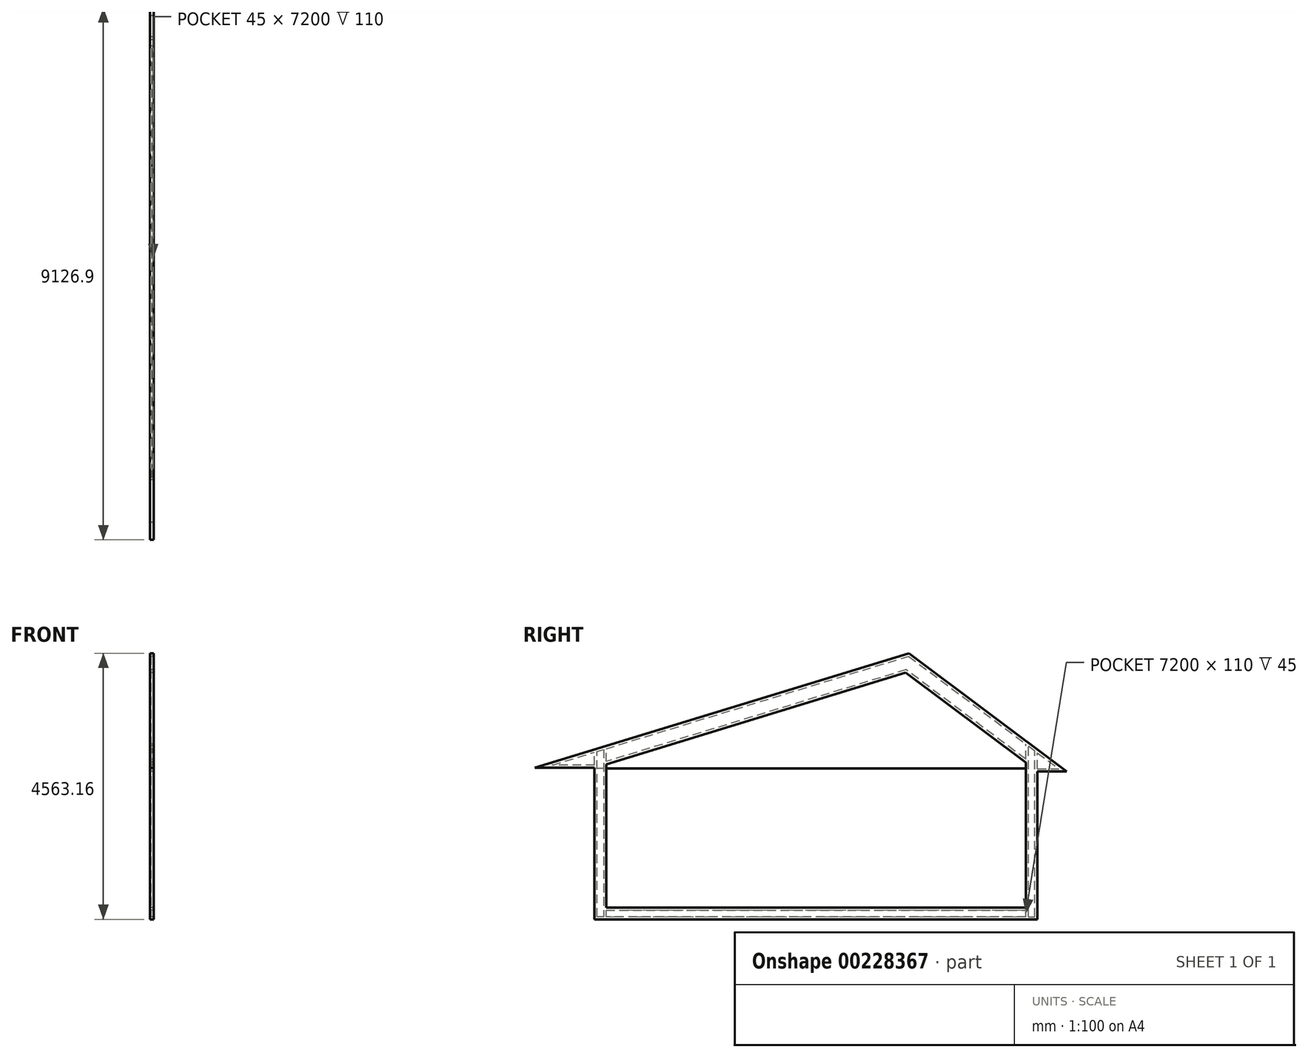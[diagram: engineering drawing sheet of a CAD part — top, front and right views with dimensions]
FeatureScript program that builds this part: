
annotation { "Feature Type Name" : "Feature", "Feature Type Description" : "" }
export const myFeature = defineFeature(function(context is Context, id is Id, definition is map)
    precondition{}
    {
        {
            var Q0;
            Q0=qCreatedBy(makeId("Right.planeOp"),FACE);
            var sketch = newSketch(context, id + "F0", { "sketchPlane" : qUnion([Q0])});
            skLineSegment(sketch, "E0", {"start": v(0, 0) * mm, "end": v(0, 2913.7) * mm});
            skLineSegment(sketch, "E1", {"start": v(0, 2913.7) * mm, "end": v(5395.13, 4563.16) * mm});
            skLineSegment(sketch, "E2", {"start": v(5395.13, 4563.16) * mm, "end": v(7600, 2913.7) * mm});
            skLineSegment(sketch, "E3", {"start": v(7600, 2913.7) * mm, "end": v(7600, 0) * mm});
            skLineSegment(sketch, "E4", {"start": v(7600, 0) * mm, "end": v(0, 0) * mm});
            skLineSegment(sketch, "E5", {"start": v(200, 200) * mm, "end": v(200, 2661.15) * mm});
            skLineSegment(sketch, "E6", {"start": v(200, 2661.15) * mm, "end": v(5337.3, 4231.77) * mm});
            skLineSegment(sketch, "E7", {"start": v(5337.3, 4231.77) * mm, "end": v(7400, 2688.67) * mm});
            skLineSegment(sketch, "E8", {"start": v(7400, 2688.67) * mm, "end": v(7400, 200) * mm});
            skLineSegment(sketch, "E9", {"start": v(7400, 200) * mm, "end": v(200, 200) * mm});
            skLineSegment(sketch, "E10", {"start": v(0, 2913.7) * mm, "end": v(-1026.1, 2600) * mm});
            skLineSegment(sketch, "E11", {"start": v(-1026.1, 2600) * mm, "end": v(0, 2600) * mm});
            skLineSegment(sketch, "E12", {"start": v(7600, 2913.7) * mm, "end": v(8100.81, 2539.05) * mm});
            skLineSegment(sketch, "E13", {"start": v(8100.81, 2539.05) * mm, "end": v(7600, 2539.05) * mm});
            skSolve(sketch);
        }
        {
            var Q0;
            Q0 = qSketchRegion(id + "F0", true);
            extrude(context, id + "F1", {"entities" : qUnion([Q0]), "depth" : 10 * mm, "offsetDistance" : 25 * mm});
        }
        {
            var Q0;
            Q0=makeQuery(id+"F1.opExtrude","CAP_FACE",FACE,{"disambiguationData":[OSD([sQuery(id+"F0.wireOp",EDGE,"E0"),sQuery(id+"F0.wireOp",EDGE,"E1"),sQuery(id+"F0.wireOp",EDGE,"E2"),sQuery(id+"F0.wireOp",EDGE,"E3"),sQuery(id+"F0.wireOp",EDGE,"E4"),sQuery(id+"F0.wireOp",EDGE,"E5"),sQuery(id+"F0.wireOp",EDGE,"E6"),sQuery(id+"F0.wireOp",EDGE,"E7"),sQuery(id+"F0.wireOp",EDGE,"E8"),sQuery(id+"F0.wireOp",EDGE,"E9"),sQuery(id+"F0.wireOp",EDGE,"E10"),sQuery(id+"F0.wireOp",EDGE,"E11"),sQuery(id+"F0.wireOp",EDGE,"E12"),sQuery(id+"F0.wireOp",EDGE,"E13")])],"isStart":false});
            var sketch = newSketch(context, id + "F2", { "sketchPlane" : qUnion([Q0])});
            skLineSegment(sketch, "E14", {"start": v(-872.18, 2600) * mm, "end": v(5386.45, 4513.45) * mm});
            skLineSegment(sketch, "E15", {"start": v(5386.45, 4513.45) * mm, "end": v(8025.7, 2539.05) * mm});
            skLineSegment(sketch, "E16", {"start": v(45, 0) * mm, "end": v(45, 2880.4) * mm});
            skLineSegment(sketch, "E17", {"start": v(155, 2914.04) * mm, "end": v(155, 0) * mm});
            skLineSegment(sketch, "E18", {"start": v(7445, 0) * mm, "end": v(7445, 2973.46) * mm});
            skLineSegment(sketch, "E19", {"start": v(200, 0) * mm, "end": v(200, 2927.8) * mm});
            skLineSegment(sketch, "E20", {"start": v(7400, 0) * mm, "end": v(7400, 3007.13) * mm});
            skLineSegment(sketch, "E21", {"start": v(7555, 0) * mm, "end": v(7555, 2891.17) * mm});
            skLineSegment(sketch, "E22", {"start": v(7600, 2539.05) * mm, "end": v(7600, 2857.5) * mm});
            skLineSegment(sketch, "E23", {"start": v(0, 2600) * mm, "end": v(0, 2866.65) * mm});
            skLineSegment(sketch, "E24", {"start": v(0, 2645) * mm, "end": v(-724.99, 2645) * mm});
            skLineSegment(sketch, "E25", {"start": v(7600, 2584.05) * mm, "end": v(7965.54, 2584.05) * mm});
            skLineSegment(sketch, "E26", {"start": v(7400, 2744.87) * mm, "end": v(5345.97, 4281.48) * mm});
            skLineSegment(sketch, "E27", {"start": v(5345.97, 4281.48) * mm, "end": v(200, 2708.2) * mm});
            skLineSegment(sketch, "E28", {"start": v(200, 155) * mm, "end": v(7400, 155) * mm});
            skLineSegment(sketch, "E29", {"start": v(7400, 45) * mm, "end": v(200, 45) * mm});
            skLineSegment(sketch, "E30", {"start": v(5337.3, 4231.77) * mm, "end": v(5345.97, 4281.48) * mm});
            skLineSegment(sketch, "E31", {"start": v(5386.45, 4513.45) * mm, "end": v(5395.13, 4563.16) * mm});
            skLineSegment(sketch, "E32", {"start": v(155, 45) * mm, "end": v(45, 45) * mm});
            skLineSegment(sketch, "E33", {"start": v(7400, 45) * mm, "end": v(7555, 45) * mm});
            skSolve(sketch);
        }
        {
            var Q0;
            {var subQ3=sQuery(id+"F2.wireOp",EDGE,"E24");Q0=makeQuery(id+"F2.imprint","IMPRINT",FACE,{"disambiguationData":[TD([[makeQuery(id+"F2.imprint","IMPRINT",EDGE,{"derivedFrom":subQ3}),1.0]])]});}
            var Q1;
            {var subQ8=sQuery(id+"F2.wireOp",EDGE,"E31");Q1=makeQuery(id+"F2.imprint","IMPRINT",FACE,{"disambiguationData":[TD([[makeQuery(id+"F2.imprint","IMPRINT",EDGE,{"derivedFrom":subQ8}),1.0]])]});}
            var Q2;
            {var subQ5=sQuery(id+"F2.wireOp",EDGE,"E16");Q2=makeQuery(id+"F2.imprint","IMPRINT",FACE,{"disambiguationData":[TD([[makeQuery(id+"F2.imprint","IMPRINT",EDGE,{"derivedFrom":subQ5}),1.0]])]});}
            var Q3;
            {var subQ5=sQuery(id+"F2.wireOp",EDGE,"E17");Q3=makeQuery(id+"F2.imprint","IMPRINT",FACE,{"disambiguationData":[TD([[makeQuery(id+"F2.imprint","IMPRINT",EDGE,{"derivedFrom":subQ5}),1.0]])]});}
            var Q4;
            {var subQ2=sQuery(id+"F2.wireOp",EDGE,"E27");Q4=makeQuery(id+"F2.imprint","IMPRINT",FACE,{"disambiguationData":[TD([[makeQuery(id+"F2.imprint","IMPRINT",EDGE,{"derivedFrom":subQ2}),1.0]])]});}
            var Q5;
            {var subQ2=sQuery(id+"F2.wireOp",EDGE,"E28");Q5=makeQuery(id+"F2.imprint","IMPRINT",FACE,{"disambiguationData":[TD([[makeQuery(id+"F2.imprint","IMPRINT",EDGE,{"derivedFrom":subQ2}),1.0]])]});}
            var Q6;
            {var subQ3=sQuery(id+"F2.wireOp",EDGE,"E29");Q6=makeQuery(id+"F2.imprint","IMPRINT",FACE,{"disambiguationData":[TD([[makeQuery(id+"F2.imprint","IMPRINT",EDGE,{"derivedFrom":subQ3}),1.0]])]});}
            var Q7;
            {var subQ2=sQuery(id+"F2.wireOp",EDGE,"E26");Q7=makeQuery(id+"F2.imprint","IMPRINT",FACE,{"disambiguationData":[TD([[makeQuery(id+"F2.imprint","IMPRINT",EDGE,{"derivedFrom":subQ2}),1.0]])]});}
            var Q8;
            {var subQ6=sQuery(id+"F2.wireOp",EDGE,"E31");Q8=makeQuery(id+"F2.imprint","IMPRINT",FACE,{"disambiguationData":[TD([[makeQuery(id+"F2.imprint","IMPRINT",EDGE,{"derivedFrom":subQ6}),-1.0]])]});}
            var Q9;
            {var subQ4=sQuery(id+"F2.wireOp",EDGE,"E18");Q9=makeQuery(id+"F2.imprint","IMPRINT",FACE,{"disambiguationData":[TD([[makeQuery(id+"F2.imprint","IMPRINT",EDGE,{"derivedFrom":subQ4}),1.0]])]});}
            var Q10;
            {var subQ3=sQuery(id+"F2.wireOp",EDGE,"E21");Q10=makeQuery(id+"F2.imprint","IMPRINT",FACE,{"disambiguationData":[TD([[makeQuery(id+"F2.imprint","IMPRINT",EDGE,{"derivedFrom":subQ3}),-1.0]])]});}
            var Q11;
            {var subQ3=sQuery(id+"F2.wireOp",EDGE,"E25");Q11=makeQuery(id+"F2.imprint","IMPRINT",FACE,{"disambiguationData":[TD([[makeQuery(id+"F2.imprint","IMPRINT",EDGE,{"derivedFrom":subQ3}),-1.0]])]});}
            var Q12;
            {var subQ5=sQuery(id+"F2.wireOp",EDGE,"E18");var subQ6=sQuery(id+"F2.wireOp",EDGE,"E15");var subQ7=makeQuery(id+"F2.imprint","INTERSECT",VERTEX,{"derivedFrom":[subQ6,subQ5]});Q12=makeQuery(id+"F2.imprint","IMPRINT",FACE,{"disambiguationData":[TD([[makeQuery(id+"F2.imprint","IMPRINT",EDGE,{"disambiguationData":[TD([[subQ7,1.0]])],"derivedFrom":subQ6}),-1.0]])]});}
            var Q13;
            {var subQ0=sQuery(id+"F2.wireOp",EDGE,"E18");var subQ1=makeQuery(id+"F1.opExtrude","CAP_EDGE",EDGE,{"disambiguationData":[OSD([sQuery(id+"F0.wireOp",EDGE,"E4")])],"isStart":false});var subQ2=makeQuery(id+"F2.imprint","INTERSECT",VERTEX,{"derivedFrom":[subQ1,subQ0]});Q13=makeQuery(id+"F2.imprint","IMPRINT",FACE,{"disambiguationData":[TD([[makeQuery(id+"F2.imprint","IMPRINT",EDGE,{"disambiguationData":[TD([[subQ2,-1.0]])],"derivedFrom":subQ0}),-1.0]])]});}
            var Q14;
            {var subQ3=sQuery(id+"F2.wireOp",EDGE,"E32");Q14=makeQuery(id+"F2.imprint","IMPRINT",FACE,{"disambiguationData":[TD([[makeQuery(id+"F2.imprint","IMPRINT",EDGE,{"derivedFrom":subQ3}),1.0]])]});}
            extrude(context, id + "F3", {"entities" : qUnion([Q0, Q1, Q2, Q3, Q4, Q5, Q6, Q7, Q8, Q9, Q10, Q11, Q12, Q13, Q14]), "operationType" : NewBodyOperationType.ADD, "depth" : 45 * mm, "offsetDistance" : 25 * mm});
        }
        {
            var Q0;
            Q0=makeQuery(id+"F3.opExtrude","CAP_FACE",FACE,{"disambiguationData":[OSD([sQuery(id+"F0.wireOp",EDGE,"E0"),sQuery(id+"F0.wireOp",EDGE,"E1"),sQuery(id+"F0.wireOp",EDGE,"E2"),sQuery(id+"F0.wireOp",EDGE,"E3"),sQuery(id+"F0.wireOp",EDGE,"E4"),sQuery(id+"F0.wireOp",EDGE,"E6"),sQuery(id+"F0.wireOp",EDGE,"E7"),sQuery(id+"F0.wireOp",EDGE,"E9"),sQuery(id+"F0.wireOp",EDGE,"E10"),sQuery(id+"F0.wireOp",EDGE,"E11"),sQuery(id+"F0.wireOp",EDGE,"E12"),sQuery(id+"F0.wireOp",EDGE,"E13"),sQuery(id+"F2.wireOp",EDGE,"E14"),sQuery(id+"F2.wireOp",EDGE,"E15"),sQuery(id+"F2.wireOp",EDGE,"E16"),sQuery(id+"F2.wireOp",EDGE,"E17"),sQuery(id+"F2.wireOp",EDGE,"E18"),sQuery(id+"F2.wireOp",EDGE,"E19"),sQuery(id+"F2.wireOp",EDGE,"E20"),sQuery(id+"F2.wireOp",EDGE,"E21"),sQuery(id+"F2.wireOp",EDGE,"E22"),sQuery(id+"F2.wireOp",EDGE,"E23"),sQuery(id+"F2.wireOp",EDGE,"E24"),sQuery(id+"F2.wireOp",EDGE,"E25"),sQuery(id+"F2.wireOp",EDGE,"E26"),sQuery(id+"F2.wireOp",EDGE,"E27"),sQuery(id+"F2.wireOp",EDGE,"E28"),sQuery(id+"F2.wireOp",EDGE,"E29")])],"isStart":false});
            var sketch = newSketch(context, id + "F4", { "sketchPlane" : qUnion([Q0])});
            skSolve(sketch);
        }
        {
            var Q0;
            {var subQ0=sQuery(id+"F2.wireOp",EDGE,"E23");Q0=makeQuery(id+"F4.imprint","IMPRINT",FACE,{"disambiguationData":[TD([[makeQuery(id+"F4.imprint","IMPRINT",EDGE,{"derivedFrom":makeQuery(id+"F3.opExtrude","CAP_EDGE",EDGE,{"disambiguationData":[OSD([subQ0])],"isStart":false})}),1.0]])]});}
            var Q1;
            {var subQ21=sQuery(id+"F2.wireOp",EDGE,"E16");Q1=makeQuery(id+"F4.imprint","IMPRINT",FACE,{"disambiguationData":[TD([[makeQuery(id+"F4.imprint","IMPRINT",EDGE,{"derivedFrom":makeQuery(id+"F3.opExtrude","CAP_EDGE",EDGE,{"disambiguationData":[OSD([subQ21])],"isStart":false})}),1.0]])]});}
            var Q2;
            {var subQ0=sQuery(id+"F2.wireOp",EDGE,"E16");Q2=makeQuery(id+"F4.imprint","IMPRINT",FACE,{"disambiguationData":[TD([[makeQuery(id+"F4.imprint","IMPRINT",EDGE,{"derivedFrom":makeQuery(id+"F3.opExtrude","CAP_EDGE",EDGE,{"disambiguationData":[OSD([subQ0])],"isStart":false})}),-1.0]])]});}
            var Q3;
            {var subQ3=sQuery(id+"F2.wireOp",EDGE,"E26");Q3=makeQuery(id+"F4.imprint","IMPRINT",FACE,{"disambiguationData":[TD([[makeQuery(id+"F4.imprint","IMPRINT",EDGE,{"derivedFrom":makeQuery(id+"F3.opExtrude","CAP_EDGE",EDGE,{"disambiguationData":[OSD([subQ3])],"isStart":false})}),-1.0]])]});}
            var Q4;
            {var subQ0=sQuery(id+"F2.wireOp",EDGE,"E18");Q4=makeQuery(id+"F4.imprint","IMPRINT",FACE,{"disambiguationData":[TD([[makeQuery(id+"F4.imprint","IMPRINT",EDGE,{"derivedFrom":makeQuery(id+"F3.opExtrude","CAP_EDGE",EDGE,{"disambiguationData":[OSD([subQ0])],"isStart":false})}),-1.0]])]});}
            var Q5;
            {var subQ0=sQuery(id+"F2.wireOp",EDGE,"E22");Q5=makeQuery(id+"F4.imprint","IMPRINT",FACE,{"disambiguationData":[TD([[makeQuery(id+"F4.imprint","IMPRINT",EDGE,{"derivedFrom":makeQuery(id+"F3.opExtrude","CAP_EDGE",EDGE,{"disambiguationData":[OSD([subQ0])],"isStart":false})}),-1.0]])]});}
            var Q6;
            {var subQ0=sQuery(id+"F2.wireOp",EDGE,"E28");Q6=makeQuery(id+"F4.imprint","IMPRINT",FACE,{"disambiguationData":[TD([[makeQuery(id+"F4.imprint","IMPRINT",EDGE,{"derivedFrom":makeQuery(id+"F3.opExtrude","CAP_EDGE",EDGE,{"disambiguationData":[OSD([subQ0])],"isStart":false})}),-1.0]])]});}
            extrude(context, id + "F5", {"entities" : qUnion([Q0, Q1, Q2, Q3, Q4, Q5, Q6]), "operationType" : NewBodyOperationType.ADD, "depth" : 10 * mm, "offsetDistance" : 25 * mm});
        }
        {
            var Q0;
            {var subQ0=sQuery(id+"F0.wireOp",EDGE,"E0");Q0=makeQuery(id+"F5.boolean.opBoolean","MERGE",FACE,{"derivedFrom":[makeQuery(id+"F3.boolean.opBoolean","MERGE",FACE,{"derivedFrom":[makeQuery(id+"F1.opExtrude","SWEPT_FACE",FACE,{"disambiguationData":[OSD([subQ0])]}),makeQuery(id+"F3.opExtrude","SWEPT_FACE",FACE,{"disambiguationData":[OSD([subQ0])]})]}),makeQuery(id+"F5.opExtrude","SWEPT_FACE",FACE,{"disambiguationData":[OSD([subQ0])]})]});}
            var sketch = newSketch(context, id + "F6", { "sketchPlane" : qUnion([Q0])});
            skCircle(sketch, "E34", {"center": v(35, 2590) * mm, "radius": 1.25 * mm});
            skSolve(sketch);
        }
        {
            var Q0;
            Q0 = qSketchRegion(id + "F6", true);
            var Q1;
            {var subQ0=sQuery(id+"F2.wireOp",EDGE,"E20");Q1=makeQuery(id+"F5.boolean.opBoolean","MERGE",FACE,{"derivedFrom":[makeQuery(id+"F3.boolean.opBoolean","MERGE",FACE,{"derivedFrom":[makeQuery(id+"F1.opExtrude","SWEPT_FACE",FACE,{"disambiguationData":[OSD([sQuery(id+"F0.wireOp",EDGE,"E8")])]}),makeQuery(id+"F3.opExtrude","SWEPT_FACE",FACE,{"disambiguationData":[OSD([subQ0]),TDD([makeQuery(id+"F2.imprint","IMPRINT",EDGE,{"disambiguationData":[TD([[makeQuery(id+"F2.imprint","INTERSECT",VERTEX,{"derivedFrom":[makeQuery(id+"F1.opExtrude","CAP_EDGE",EDGE,{"disambiguationData":[OSD([sQuery(id+"F0.wireOp",EDGE,"E7")])],"isStart":false}),subQ0]}),-1.0],[makeQuery(id+"F2.imprint","INTERSECT",VERTEX,{"derivedFrom":[makeQuery(id+"F1.opExtrude","CAP_EDGE",EDGE,{"disambiguationData":[OSD([sQuery(id+"F0.wireOp",EDGE,"E9")])],"isStart":false}),subQ0]}),1.0]])],"derivedFrom":subQ0})])]})]}),makeQuery(id+"F5.opExtrude","SWEPT_FACE",FACE,{"disambiguationData":[OSD([subQ0])]})]});}
            extrude(context, id + "F7", {"entities" : qUnion([Q0]), "operationType" : NewBodyOperationType.ADD, "endBound" : BoundingType.UP_TO_SURFACE, "oppositeDirection" : true, "depth" : 25 * mm, "endBoundEntityFace" : qUnion([Q1]), "offsetDistance" : 25 * mm});
        }
    });
